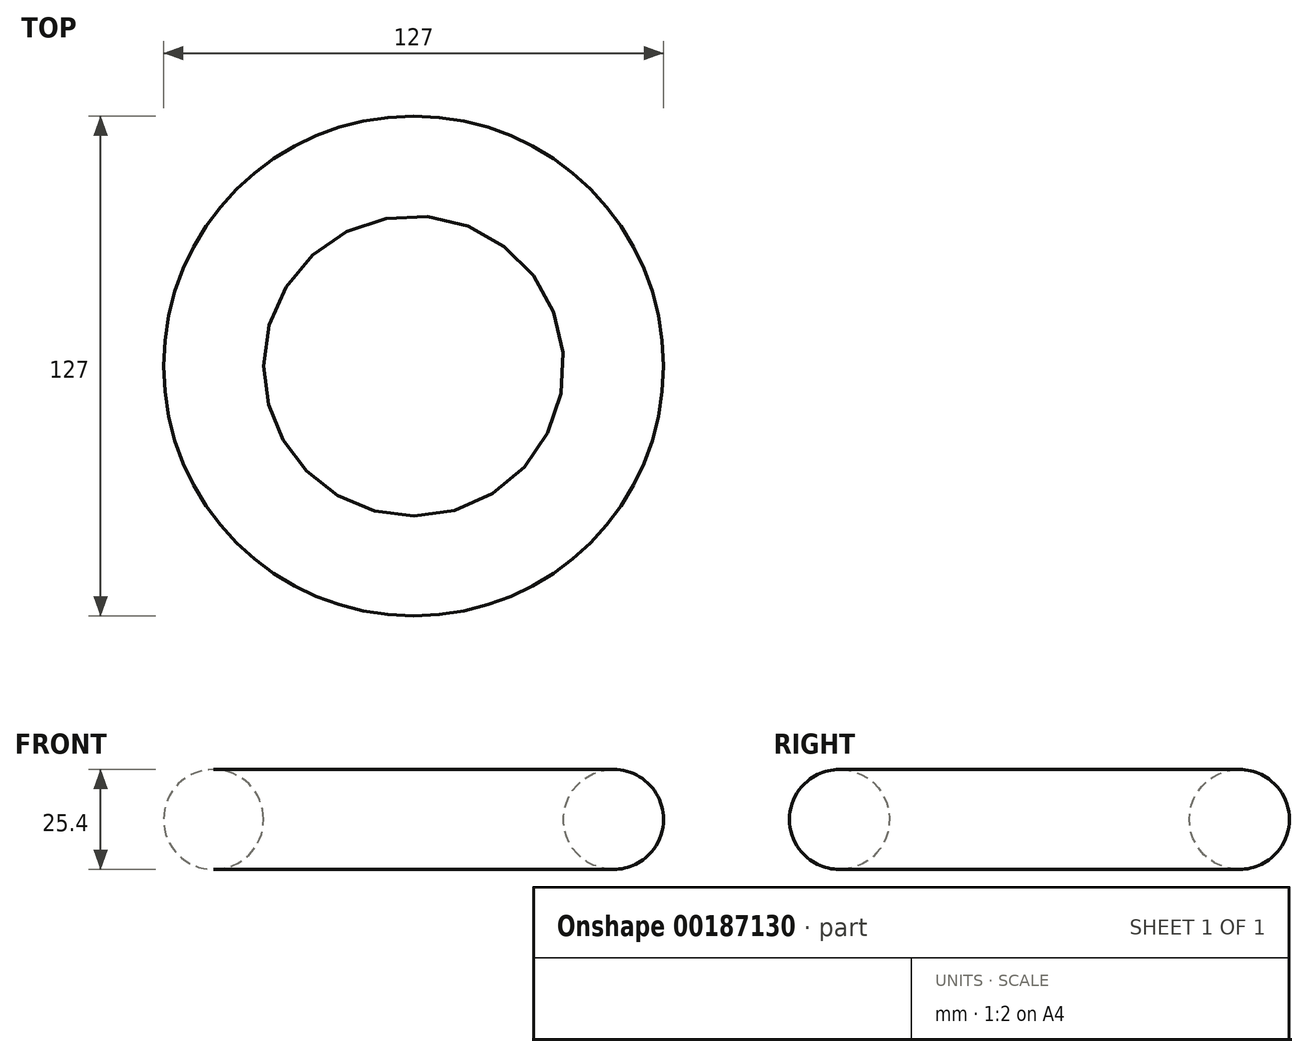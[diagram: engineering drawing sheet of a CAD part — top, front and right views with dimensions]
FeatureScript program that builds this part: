
annotation { "Feature Type Name" : "Feature", "Feature Type Description" : "" }
export const myFeature = defineFeature(function(context is Context, id is Id, definition is map)
    precondition{}
    {
        {
            var Q0;
            Q0=qCreatedBy(makeId("Front.planeOp"),FACE);
            var sketch = newSketch(context, id + "F0", { "sketchPlane" : qUnion([Q0])});
            skCircle(sketch, "E0", {"center": v(50.8, 0) * mm, "radius": 12.7 * mm});
            skLineSegment(sketch, "E1", {"start": v(0, 0) * mm, "end": v(0, 26.38) * mm});
            skSolve(sketch);
        }
        {
            var Q0;
            Q0=makeQuery(id+"F0.imprint","IMPRINT",FACE,{"disambiguationData":[TD([[makeQuery(id+"F0.imprint","IMPRINT",EDGE,{"derivedFrom":sQuery(id+"F0.wireOp",EDGE,"E0")}),1.0]])]});
            var Q1;
            Q1=sQuery(id+"F0.wireOp",EDGE,"E1");
            revolve(context, id + "F1", {"entities" : qUnion([Q0]), "axis" : qUnion([Q1]), "revolveType" : RevolveType.FULL});
        }
    });
